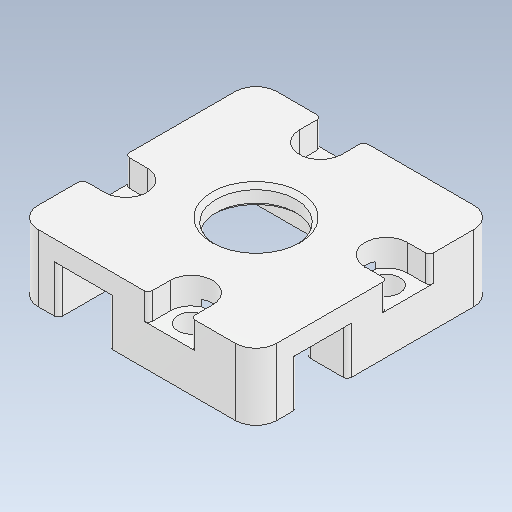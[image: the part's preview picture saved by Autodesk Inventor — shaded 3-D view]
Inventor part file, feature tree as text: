
AUTODESK INVENTOR PART (.ipt)
format: ipt  version: 2020 (Build 240168000, 168)  size: 165,888 bytes
history: native  units: in
note: dims shown in document units (in); Inventor stores cm internally (conversion verified against a paired STEP export)
features: fillet x1
ambient origin geometry x8: Origin, YZ Plane, XZ Plane, XY Plane, X Axis, Y Axis, Z Axis, Center Point
bodies: Solid1 (feature_tree)
feature tree (1):
  fillet  "Fillet4"  [1 undecoded]
note: 1 required parameter value undecoded (feature->parameter linkage not recoverable at this tier; creation-order binding heuristic only, values carry confidence <= 0.55)
